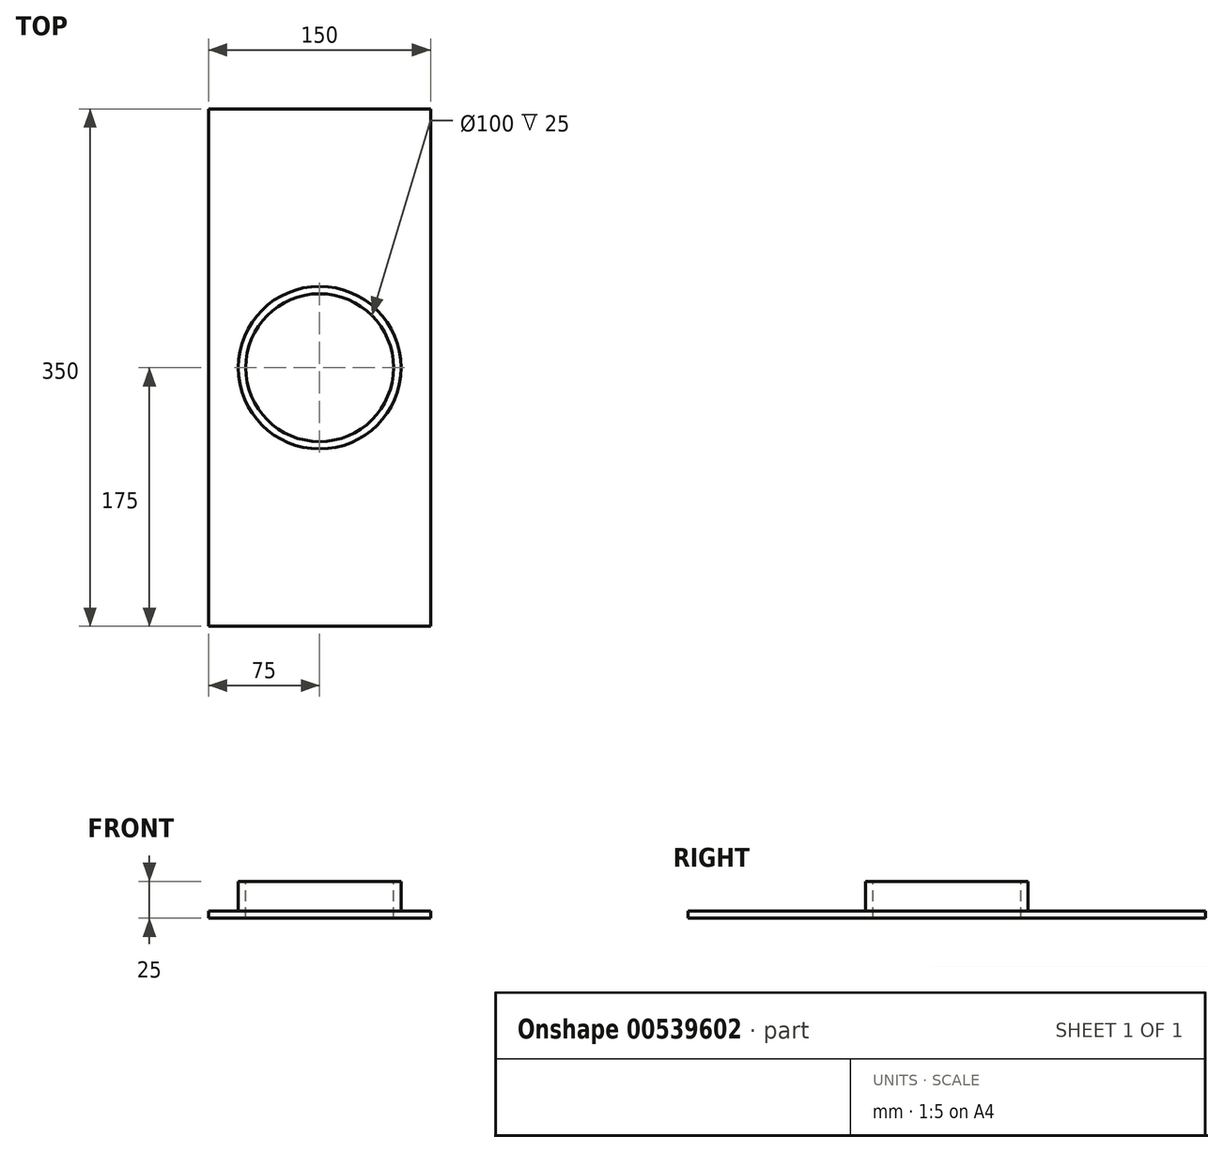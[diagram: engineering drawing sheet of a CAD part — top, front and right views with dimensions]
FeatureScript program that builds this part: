
annotation { "Feature Type Name" : "Feature", "Feature Type Description" : "" }
export const myFeature = defineFeature(function(context is Context, id is Id, definition is map)
    precondition{}
    {
        {
            var Q0;
            Q0=qCreatedBy(makeId("Top.planeOp"),FACE);
            var sketch = newSketch(context, id + "F0", { "sketchPlane" : qUnion([Q0])});
            skLineSegment(sketch, "E0.bottom", {"start": v(-75, 175) * mm, "end": v(75, 175) * mm});
            skLineSegment(sketch, "E0.top", {"start": v(-75, -175) * mm, "end": v(75, -175) * mm});
            skLineSegment(sketch, "E0.left", {"start": v(-75, 175) * mm, "end": v(-75, -175) * mm});
            skLineSegment(sketch, "E0.right", {"start": v(75, 175) * mm, "end": v(75, -175) * mm});
            skPoint(sketch, "E0.middle", {"position": v(0, 0) * mm});
            skSolve(sketch);
        }
        {
            var Q0;
            Q0=makeQuery(id+"F0.imprint","IMPRINT",FACE,{"disambiguationData":[TD([[makeQuery(id+"F0.imprint","IMPRINT",EDGE,{"derivedFrom":sQuery(id+"F0.wireOp",EDGE,"E0.bottom")}),-1.0]])]});
            extrude(context, id + "F1", {"entities" : qUnion([Q0]), "depth" : 5 * mm, "offsetDistance" : 25 * mm});
        }
        {
            var Q0;
            Q0=makeQuery(id+"F1.opExtrude","CAP_FACE",FACE,{"disambiguationData":[OSD([sQuery(id+"F0.wireOp",EDGE,"E0.bottom"),sQuery(id+"F0.wireOp",EDGE,"E0.top"),sQuery(id+"F0.wireOp",EDGE,"E0.left"),sQuery(id+"F0.wireOp",EDGE,"E0.right")])],"isStart":false});
            var sketch = newSketch(context, id + "F2", { "sketchPlane" : qUnion([Q0])});
            skCircle(sketch, "E1", {"center": v(0, 0) * mm, "radius": 50 * mm});
            skCircle(sketch, "E2", {"center": v(0, 0) * mm, "radius": 55 * mm});
            skSolve(sketch);
        }
        {
            var Q0;
            Q0=makeQuery(id+"F2.imprint","IMPRINT",FACE,{"disambiguationData":[TD([[makeQuery(id+"F2.imprint","IMPRINT",EDGE,{"derivedFrom":sQuery(id+"F2.wireOp",EDGE,"E1")}),1.0]])]});
            extrude(context, id + "F3", {"entities" : qUnion([Q0]), "operationType" : NewBodyOperationType.REMOVE, "endBound" : BoundingType.UP_TO_NEXT, "oppositeDirection" : true, "depth" : 25 * mm, "offsetDistance" : 25 * mm});
        }
        {
            var Q0;
            Q0=makeQuery(id+"F2.imprint","IMPRINT",FACE,{"disambiguationData":[TD([[makeQuery(id+"F2.imprint","IMPRINT",EDGE,{"derivedFrom":sQuery(id+"F2.wireOp",EDGE,"E1")}),-1.0]])]});
            extrude(context, id + "F4", {"entities" : qUnion([Q0]), "operationType" : NewBodyOperationType.ADD, "depth" : 20 * mm, "offsetDistance" : 25 * mm});
        }
    });
